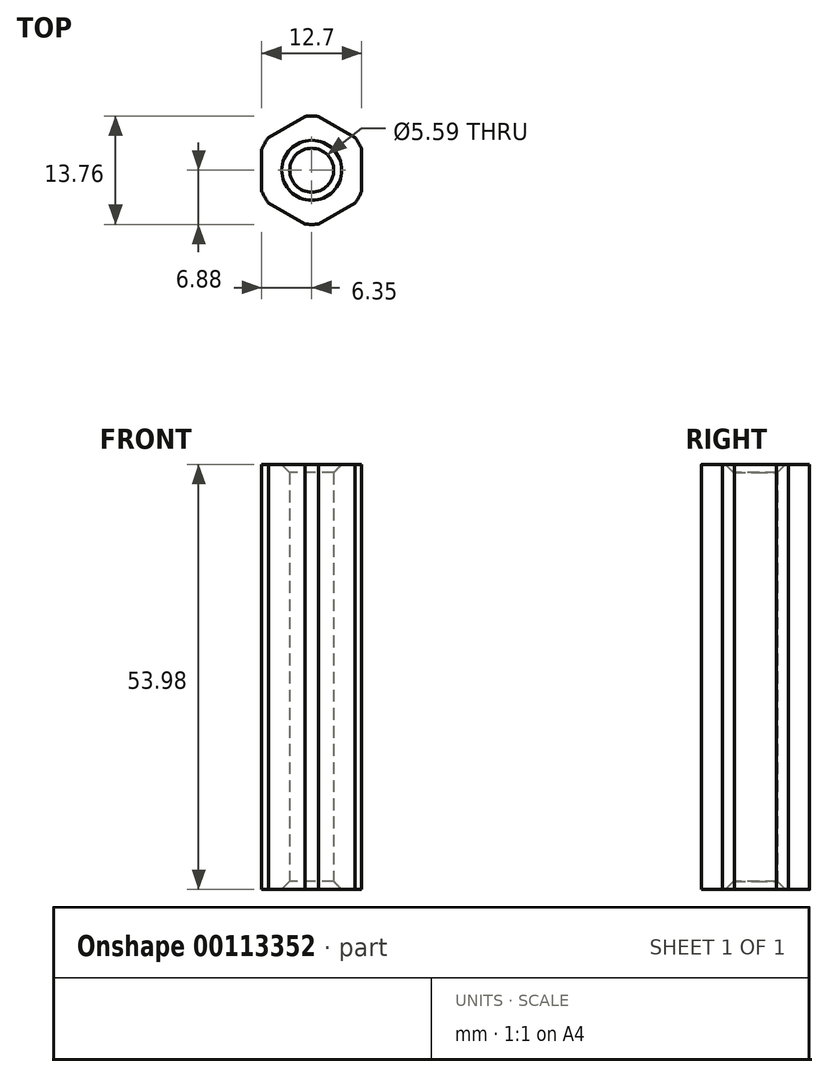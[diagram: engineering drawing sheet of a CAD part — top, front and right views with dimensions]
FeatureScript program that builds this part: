
annotation { "Feature Type Name" : "Feature", "Feature Type Description" : "" }
export const myFeature = defineFeature(function(context is Context, id is Id, definition is map)
    precondition{}
    {
        {
            var Q0;
            Q0=qCreatedBy(makeId("Top.planeOp"),FACE);
            var sketch = newSketch(context, id + "F0", { "sketchPlane" : qUnion([Q0])});
            skCircle(sketch, "E0.cCircle", {"center": v(0, 0) * mm, "radius": 6.35 * mm, "construction": true});
            skLineSegment(sketch, "E0.0", {"start": v(6.35, 3.67) * mm, "end": v(6.35, -3.67) * mm});
            skLineSegment(sketch, "E0.1", {"start": v(6.35, -3.67) * mm, "end": v(0, -7.33) * mm});
            skLineSegment(sketch, "E0.2", {"start": v(0, -7.33) * mm, "end": v(-6.35, -3.67) * mm});
            skLineSegment(sketch, "E0.3", {"start": v(-6.35, -3.67) * mm, "end": v(-6.35, 3.67) * mm});
            skLineSegment(sketch, "E0.4", {"start": v(-6.35, 3.67) * mm, "end": v(0, 7.33) * mm});
            skLineSegment(sketch, "E0.5", {"start": v(0, 7.33) * mm, "end": v(6.35, 3.67) * mm});
            skPoint(sketch, "E0.0.midPoint", {"position": v(6.35, 0) * mm});
            skCircle(sketch, "E1", {"center": v(0, 0) * mm, "radius": 2.8 * mm});
            skCircle(sketch, "E2", {"center": v(0, 0) * mm, "radius": 6.88 * mm});
            skSolve(sketch);
        }
        {
            var Q0;
            Q0=makeQuery(id+"F0.imprint","IMPRINT",FACE,{"disambiguationData":[TD([[makeQuery(id+"F0.imprint","IMPRINT",EDGE,{"derivedFrom":sQuery(id+"F0.wireOp",EDGE,"E1")}),-1.0]])]});
            extrude(context, id + "F1", {"entities" : qUnion([Q0]), "depth" : 53.97 * mm, "offsetDistance" : 25.4 * mm});
        }
        {
            var Q0;
            Q0=makeQuery(id+"F1.opExtrude","CAP_EDGE",EDGE,{"disambiguationData":[OSD([sQuery(id+"F0.wireOp",EDGE,"E1")])],"isStart":false});
            var Q1;
            Q1=makeQuery(id+"F1.opExtrude","CAP_EDGE",EDGE,{"disambiguationData":[OSD([sQuery(id+"F0.wireOp",EDGE,"E1")])],"isStart":true});
            chamfer(context, id + "F2", {"entities" : qUnion([Q0, Q1]), "width" : 1.02 * mm, "tangentPropagation" : true});
        }
    });
